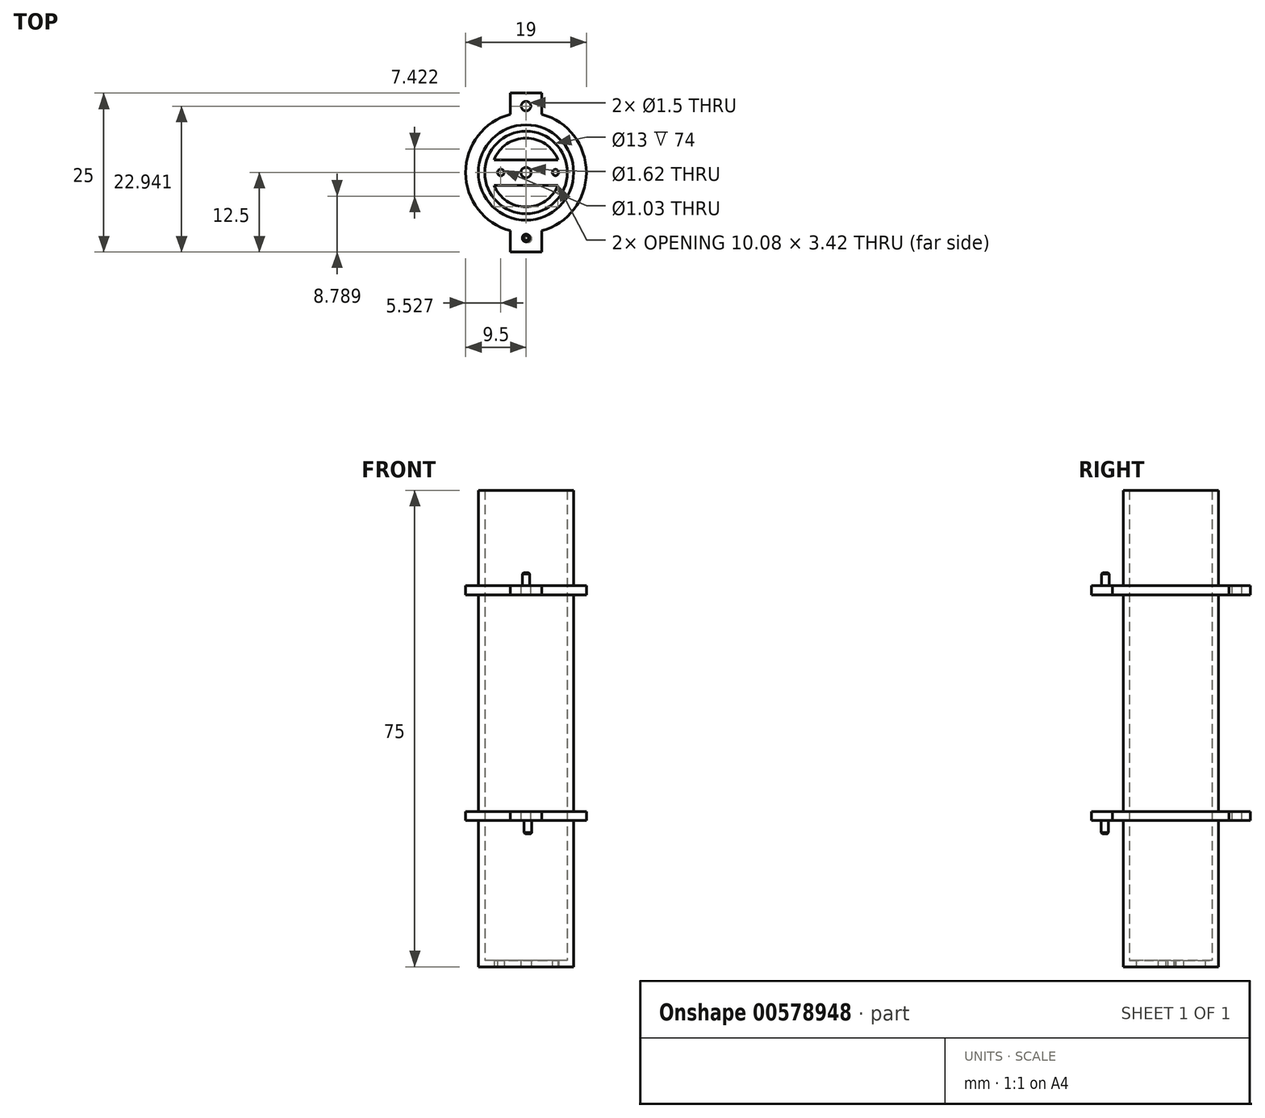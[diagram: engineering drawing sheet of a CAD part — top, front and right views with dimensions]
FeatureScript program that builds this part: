
annotation { "Feature Type Name" : "Feature", "Feature Type Description" : "" }
export const myFeature = defineFeature(function(context is Context, id is Id, definition is map)
    precondition{}
    {
        {
            var Q0;
            Q0=qCreatedBy(makeId("Top.planeOp"),FACE);
            var sketch = newSketch(context, id + "F0", { "sketchPlane" : qUnion([Q0])});
            skCircle(sketch, "E0", {"center": v(0, 0) * mm, "radius": 7.5 * mm});
            skSolve(sketch);
        }
        {
            var Q0;
            Q0 = qSketchRegion(id + "F0", true);
            var Q1;
            Q1=makeQuery(id+"F0.imprint","IMPRINT",FACE,{"disambiguationData":[TD([[makeQuery(id+"F0.imprint","IMPRINT",EDGE,{"derivedFrom":sQuery(id+"F0.wireOp",EDGE,"E0")}),1.0]])]});
            extrude(context, id + "F1", {"entities" : qUnion([Q0, Q1]), "depth" : 75 * mm, "offsetDistance" : 25 * mm});
        }
        {
            var Q0;
            Q0=makeQuery(id+"F1.opExtrude","CAP_FACE",FACE,{"disambiguationData":[OSD([sQuery(id+"F0.wireOp",EDGE,"E0")])],"isStart":false});
            shell(context, id + "F2", {"entities" : qUnion([Q0]), "thickness" : 1 * mm});
        }
        {
            var Q0;
            Q0=makeQuery(id+"F1.opExtrude","CAP_FACE",FACE,{"disambiguationData":[OSD([sQuery(id+"F0.wireOp",EDGE,"E0")])],"isStart":true});
            var sketch = newSketch(context, id + "F3", { "sketchPlane" : qUnion([Q0])});
            skLineSegment(sketch, "E1.bottom", {"start": v(9.26, 2) * mm, "end": v(-8.34, 2) * mm});
            skLineSegment(sketch, "E1.top", {"start": v(9.26, -2) * mm, "end": v(-8.34, -2) * mm});
            skLineSegment(sketch, "E1.left", {"start": v(9.26, 2) * mm, "end": v(9.26, -2) * mm});
            skLineSegment(sketch, "E1.right", {"start": v(-8.34, 2) * mm, "end": v(-8.34, -2) * mm});
            skCircle(sketch, "E2", {"center": v(0, 0) * mm, "radius": 5.42 * mm});
            skSolve(sketch);
        }
        {
            var Q0;
            {var subQ0=sQuery(id+"F3.wireOp",EDGE,"E2");var subQ1=sQuery(id+"F3.wireOp",EDGE,"E1.bottom");var subQ2=makeQuery(id+"F3.imprint","INTERSECT",VERTEX,{"disambiguationData":[OD(0.0)],"derivedFrom":[subQ1,subQ0]});Q0=makeQuery(id+"F3.imprint","IMPRINT",FACE,{"disambiguationData":[TD([[makeQuery(id+"F3.imprint","IMPRINT",EDGE,{"disambiguationData":[TD([[subQ2,-1.0]])],"derivedFrom":subQ1}),-1.0]])]});}
            var Q1;
            {var subQ0=sQuery(id+"F3.wireOp",EDGE,"E2");var subQ1=sQuery(id+"F3.wireOp",EDGE,"E1.top");var subQ2=makeQuery(id+"F3.imprint","INTERSECT",VERTEX,{"disambiguationData":[OD(0.0)],"derivedFrom":[subQ1,subQ0]});Q1=makeQuery(id+"F3.imprint","IMPRINT",FACE,{"disambiguationData":[TD([[makeQuery(id+"F3.imprint","IMPRINT",EDGE,{"disambiguationData":[TD([[subQ2,-1.0]])],"derivedFrom":subQ1}),1.0]])]});}
            extrude(context, id + "F4", {"entities" : qUnion([Q0, Q1]), "operationType" : NewBodyOperationType.REMOVE, "oppositeDirection" : true, "depth" : 25 * mm, "offsetDistance" : 25 * mm});
        }
        {
            var Q0;
            Q0=makeQuery(id+"F1.opExtrude","CAP_FACE",FACE,{"disambiguationData":[OSD([sQuery(id+"F0.wireOp",EDGE,"E0")])],"isStart":true});
            var sketch = newSketch(context, id + "F5", { "sketchPlane" : qUnion([Q0])});
            skCircle(sketch, "E3", {"center": v(0, 0) * mm, "radius": 0.8 * mm});
            skCircle(sketch, "E4", {"center": v(-3.97, 0) * mm, "radius": 0.52 * mm});
            skCircle(sketch, "E5", {"center": v(4.64, 0) * mm, "radius": 0.49 * mm});
            skSolve(sketch);
        }
        {
            var Q0;
            Q0=sQuery(id+"F5.wireOp",VERTEX,"E3.center");
            var Q1;
            Q1=makeQuery(id+"F1.opExtrude","SWEPT_BODY",BODY,{"disambiguationData":[OSD([sQuery(id+"F0.wireOp",EDGE,"E0")])]});
            hole(context, id + "F6", {"style" : HoleStyle.SIMPLE, "endStyle" : HoleEndStyle.BLIND, "holeDiameter" : 1.5 * mm, "holeDepth" : 25 * mm, "isTappedThrough" : true, "tappedDepth" : 12 * mm, "tapClearance" : 3, "locations" : qUnion([Q0]), "scope" : qUnion([Q1])});
        }
        {
            var Q0;
            Q0 = qSketchRegion(id + "F5", true);
            extrude(context, id + "F7", {"entities" : qUnion([Q0]), "operationType" : NewBodyOperationType.REMOVE, "oppositeDirection" : true, "depth" : 25 * mm, "offsetDistance" : 25 * mm});
        }
        {
            var Q0;
            Q0=makeQuery(id+"F1.opExtrude","CAP_FACE",FACE,{"disambiguationData":[OSD([sQuery(id+"F0.wireOp",EDGE,"E0")])],"isStart":false});
            var sketch = newSketch(context, id + "F8", { "sketchPlane" : qUnion([Q0])});
            skCircle(sketch, "E6", {"center": v(0, 0) * mm, "radius": 9.5 * mm});
            skSolve(sketch);
        }
        {
            var Q0;
            Q0=makeQuery(id+"F8.imprint","IMPRINT",FACE,{"disambiguationData":[TD([[makeQuery(id+"F8.imprint","IMPRINT",EDGE,{"derivedFrom":sQuery(id+"F8.wireOp",EDGE,"E6")}),1.0]])]});
            extrude(context, id + "F9", {"entities" : qUnion([Q0]), "operationType" : NewBodyOperationType.ADD, "oppositeDirection" : true, "depth" : 52 * mm, "offsetDistance" : 25 * mm, "hasSecondDirection" : true, "secondDirectionOppositeDirection" : true, "secondDirectionDepth" : 15 * mm});
        }
        {
            var Q0;
            Q0=makeQuery(id+"F9.opExtrude","CAP_FACE",FACE,{"disambiguationData":[OSD([sQuery(id+"F0.wireOp",EDGE,"E0"),sQuery(id+"F8.wireOp",EDGE,"E6")])],"isStart":true});
            extrude(context, id + "F10", {"entities" : qUnion([Q0]), "operationType" : NewBodyOperationType.REMOVE, "oppositeDirection" : true, "depth" : 35.6 * mm, "offsetDistance" : 25 * mm, "hasSecondDirection" : true, "secondDirectionOppositeDirection" : true, "secondDirectionDepth" : 1.5 * mm});
        }
        {
            var Q0;
            Q0=makeQuery(id+"F9.opExtrude","CAP_FACE",FACE,{"disambiguationData":[OSD([sQuery(id+"F0.wireOp",EDGE,"E0"),sQuery(id+"F8.wireOp",EDGE,"E6")])],"isStart":true});
            var sketch = newSketch(context, id + "F11", { "sketchPlane" : qUnion([Q0])});
            skLineSegment(sketch, "E7.bottom", {"start": v(-2.5, 0) * mm, "end": v(2.5, 0) * mm});
            skLineSegment(sketch, "E7.top", {"start": v(-2.5, 12.5) * mm, "end": v(2.5, 12.5) * mm});
            skLineSegment(sketch, "E7.left", {"start": v(-2.5, 0) * mm, "end": v(-2.5, 12.5) * mm});
            skLineSegment(sketch, "E7.right", {"start": v(2.5, 0) * mm, "end": v(2.5, 12.5) * mm});
            skLineSegment(sketch, "E8.top", {"start": v(-2.5, -12.5) * mm, "end": v(2.5, -12.5) * mm});
            skLineSegment(sketch, "E8.left", {"start": v(-2.5, 0) * mm, "end": v(-2.5, -12.5) * mm});
            skLineSegment(sketch, "E8.right", {"start": v(2.5, 0) * mm, "end": v(2.5, -12.5) * mm});
            skSolve(sketch);
        }
        {
            var Q0;
            {var subQ0=sQuery(id+"F11.wireOp",EDGE,"E8.top");Q0=makeQuery(id+"F11.imprint","IMPRINT",FACE,{"disambiguationData":[TD([[makeQuery(id+"F11.imprint","IMPRINT",EDGE,{"derivedFrom":subQ0}),1.0]])]});}
            var Q1;
            {var subQ0=sQuery(id+"F11.wireOp",EDGE,"E7.top");Q1=makeQuery(id+"F11.imprint","IMPRINT",FACE,{"disambiguationData":[TD([[makeQuery(id+"F11.imprint","IMPRINT",EDGE,{"derivedFrom":subQ0}),-1.0]])]});}
            extrude(context, id + "F12", {"entities" : qUnion([Q0, Q1]), "operationType" : NewBodyOperationType.ADD, "oppositeDirection" : true, "depth" : 37 * mm, "offsetDistance" : 25 * mm});
        }
        {
            var Q0;
            Q0=makeQuery(id+"F12.opExtrude","SWEPT_FACE",FACE,{"disambiguationData":[OSD([sQuery(id+"F11.wireOp",EDGE,"E7.right")])]});
            var sketch = newSketch(context, id + "F13", { "sketchPlane" : qUnion([Q0])});
            skLineSegment(sketch, "E9.bottom", {"start": v(9.17, 24.4) * mm, "end": v(12.5, 24.4) * mm});
            skLineSegment(sketch, "E9.top", {"start": v(9.17, 58.5) * mm, "end": v(12.5, 58.5) * mm});
            skLineSegment(sketch, "E9.left", {"start": v(9.17, 24.4) * mm, "end": v(9.17, 58.5) * mm});
            skLineSegment(sketch, "E9.right", {"start": v(12.5, 24.4) * mm, "end": v(12.5, 58.5) * mm});
            skLineSegment(sketch, "E10.bottom", {"start": v(-8.68, 58.5) * mm, "end": v(-13.68, 58.5) * mm});
            skLineSegment(sketch, "E10.top", {"start": v(-8.68, 24.4) * mm, "end": v(-13.68, 24.4) * mm});
            skLineSegment(sketch, "E10.left", {"start": v(-8.68, 58.5) * mm, "end": v(-8.68, 24.4) * mm});
            skLineSegment(sketch, "E10.right", {"start": v(-13.68, 58.5) * mm, "end": v(-13.68, 24.4) * mm});
            skSolve(sketch);
        }
        {
            var Q0;
            Q0=makeQuery(id+"F13.imprint","IMPRINT",FACE,{"disambiguationData":[TD([[makeQuery(id+"F13.imprint","IMPRINT",EDGE,{"derivedFrom":sQuery(id+"F13.wireOp",EDGE,"E9.bottom")}),1.0]])]});
            var Q1;
            Q1=makeQuery(id+"F13.imprint","IMPRINT",FACE,{"disambiguationData":[TD([[makeQuery(id+"F13.imprint","IMPRINT",EDGE,{"derivedFrom":sQuery(id+"F13.wireOp",EDGE,"E10.bottom")}),1.0]])]});
            extrude(context, id + "F14", {"entities" : qUnion([Q0, Q1]), "operationType" : NewBodyOperationType.REMOVE, "oppositeDirection" : true, "depth" : 25 * mm, "offsetDistance" : 25 * mm});
        }
        {
            var Q0;
            {var subQ0=sQuery(id+"F8.wireOp",EDGE,"E6");Q0=makeQuery(id+"F12.boolean.opBoolean","MERGE",FACE,{"derivedFrom":[makeQuery(id+"F9.opExtrude","CAP_FACE",FACE,{"disambiguationData":[OSD([sQuery(id+"F0.wireOp",EDGE,"E0"),subQ0])],"isStart":true}),makeQuery(id+"F12.opExtrude","CAP_FACE",FACE,{"disambiguationData":[OSD([subQ0,sQuery(id+"F11.wireOp",EDGE,"E7.top"),sQuery(id+"F11.wireOp",EDGE,"E7.left"),sQuery(id+"F11.wireOp",EDGE,"E7.right")])],"isStart":true}),makeQuery(id+"F12.opExtrude","CAP_FACE",FACE,{"disambiguationData":[OSD([subQ0,sQuery(id+"F11.wireOp",EDGE,"E8.top"),sQuery(id+"F11.wireOp",EDGE,"E8.left"),sQuery(id+"F11.wireOp",EDGE,"E8.right")])],"isStart":true})]});}
            var sketch = newSketch(context, id + "F15", { "sketchPlane" : qUnion([Q0])});
            skCircle(sketch, "E11", {"center": v(0, -10.33) * mm, "radius": 0.5 * mm});
            skCircle(sketch, "E12", {"center": v(0, 10.44) * mm, "radius": 0.75 * mm});
            skSolve(sketch);
        }
        {
            var Q0;
            Q0=sQuery(id+"F15.wireOp",VERTEX,"E12.center");
            var Q1;
            Q1=makeQuery(id+"F1.opExtrude","SWEPT_BODY",BODY,{"disambiguationData":[OSD([sQuery(id+"F0.wireOp",EDGE,"E0")])]});
            hole(context, id + "F16", {"style" : HoleStyle.SIMPLE, "endStyle" : HoleEndStyle.BLIND, "holeDiameter" : 1.5 * mm, "holeDepth" : 200 * mm, "isTappedThrough" : true, "tappedDepth" : 12 * mm, "tapClearance" : 3, "locations" : qUnion([Q0]), "scope" : qUnion([Q1])});
        }
        {
            var Q0;
            {var subQ0=sQuery(id+"F8.wireOp",EDGE,"E6");Q0=makeQuery(id+"F12.boolean.opBoolean","MERGE",FACE,{"derivedFrom":[makeQuery(id+"F9.opExtrude","CAP_FACE",FACE,{"disambiguationData":[OSD([sQuery(id+"F0.wireOp",EDGE,"E0"),subQ0])],"isStart":true}),makeQuery(id+"F12.opExtrude","CAP_FACE",FACE,{"disambiguationData":[OSD([subQ0,sQuery(id+"F11.wireOp",EDGE,"E7.top"),sQuery(id+"F11.wireOp",EDGE,"E7.left"),sQuery(id+"F11.wireOp",EDGE,"E7.right")])],"isStart":true}),makeQuery(id+"F12.opExtrude","CAP_FACE",FACE,{"disambiguationData":[OSD([subQ0,sQuery(id+"F11.wireOp",EDGE,"E8.top"),sQuery(id+"F11.wireOp",EDGE,"E8.left"),sQuery(id+"F11.wireOp",EDGE,"E8.right")])],"isStart":true})]});}
            var sketch = newSketch(context, id + "F17", { "sketchPlane" : qUnion([Q0])});
            skCircle(sketch, "E13", {"center": v(0, -10.3) * mm, "radius": 0.6 * mm});
            skSolve(sketch);
        }
        {
            var Q0;
            Q0=makeQuery(id+"F17.imprint","IMPRINT",FACE,{"disambiguationData":[TD([[makeQuery(id+"F17.imprint","IMPRINT",EDGE,{"derivedFrom":sQuery(id+"F17.wireOp",EDGE,"E13")}),1.0]])]});
            extrude(context, id + "F18", {"entities" : qUnion([Q0]), "operationType" : NewBodyOperationType.ADD, "depth" : 2 * mm, "offsetDistance" : 25 * mm});
        }
        {
            var Q0;
            Q0=makeQuery(id+"F18.opExtrude","CAP_EDGE",EDGE,{"disambiguationData":[OSD([sQuery(id+"F17.wireOp",EDGE,"E13")])],"isStart":false});
            chamfer(context, id + "F19", {"entities" : qUnion([Q0]), "width" : 0.2 * mm, "tangentPropagation" : true});
        }
        {
            var Q0;
            Q0=makeQuery(id+"F14.boolean.opBoolean","MERGE",FACE,{"derivedFrom":[makeQuery(id+"F10.boolean.opBoolean","COPY",FACE,{"derivedFrom":makeQuery(id+"F10.opExtrude","CAP_FACE",FACE,{"disambiguationData":[OSD([sQuery(id+"F0.wireOp",EDGE,"E0"),sQuery(id+"F8.wireOp",EDGE,"E6")])],"isStart":false})}),makeQuery(id+"F14.opExtrude","SWEPT_FACE",FACE,{"disambiguationData":[OSD([sQuery(id+"F13.wireOp",EDGE,"E9.bottom")])]}),makeQuery(id+"F14.opExtrude","SWEPT_FACE",FACE,{"disambiguationData":[OSD([sQuery(id+"F13.wireOp",EDGE,"E10.top")])]})]});
            var sketch = newSketch(context, id + "F20", { "sketchPlane" : qUnion([Q0])});
            skCircle(sketch, "E14", {"center": v(0.29, -10.4) * mm, "radius": 0.6 * mm});
            skSolve(sketch);
        }
        {
            var Q0;
            Q0=makeQuery(id+"F20.imprint","IMPRINT",FACE,{"disambiguationData":[TD([[makeQuery(id+"F20.imprint","IMPRINT",EDGE,{"derivedFrom":sQuery(id+"F20.wireOp",EDGE,"E14")}),1.0]])]});
            extrude(context, id + "F21", {"entities" : qUnion([Q0]), "operationType" : NewBodyOperationType.ADD, "oppositeDirection" : true, "depth" : 3.5 * mm, "offsetDistance" : 25 * mm});
        }
        {
            var Q0;
            Q0=makeQuery(id+"F21.opExtrude","CAP_EDGE",EDGE,{"disambiguationData":[OSD([sQuery(id+"F20.wireOp",EDGE,"E14")])],"isStart":false});
            chamfer(context, id + "F22", {"entities" : qUnion([Q0]), "width" : 0.2 * mm, "tangentPropagation" : true});
        }
    });
